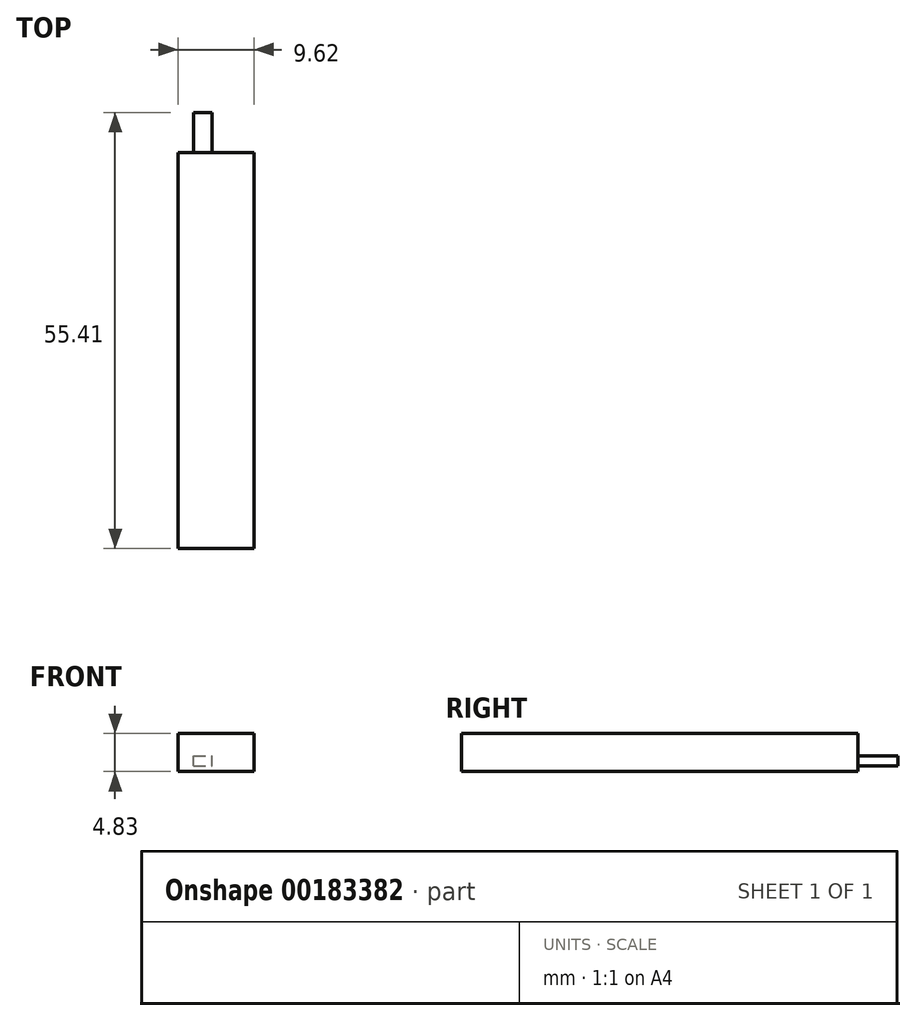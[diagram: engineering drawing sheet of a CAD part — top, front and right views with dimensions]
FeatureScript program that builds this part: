
annotation { "Feature Type Name" : "Feature", "Feature Type Description" : "" }
export const myFeature = defineFeature(function(context is Context, id is Id, definition is map)
    precondition{}
    {
        {
            var Q0;
            Q0=qCreatedBy(makeId("Top.planeOp"),FACE);
            var sketch = newSketch(context, id + "F0", { "sketchPlane" : qUnion([Q0])});
            skLineSegment(sketch, "E0.bottom", {"start": v(-36.29, 75.05) * mm, "end": v(-26.67, 75.05) * mm});
            skLineSegment(sketch, "E0.top", {"start": v(-36.29, 24.72) * mm, "end": v(-26.67, 24.72) * mm});
            skLineSegment(sketch, "E0.left", {"start": v(-36.29, 75.05) * mm, "end": v(-36.29, 24.72) * mm});
            skLineSegment(sketch, "E0.right", {"start": v(-26.67, 75.05) * mm, "end": v(-26.67, 24.72) * mm});
            skSolve(sketch);
        }
        {
            var Q0;
            Q0=makeQuery(id+"F0.imprint","IMPRINT",FACE,{"disambiguationData":[TD([[makeQuery(id+"F0.imprint","IMPRINT",EDGE,{"derivedFrom":sQuery(id+"F0.wireOp",EDGE,"E0.bottom")}),-1.0]])]});
            extrude(context, id + "F1", {"entities" : qUnion([Q0]), "depth" : 4.83 * mm});
        }
        {
            var Q0;
            Q0=makeQuery(id+"F1.opExtrude","SWEPT_FACE",FACE,{"disambiguationData":[OSD([sQuery(id+"F0.wireOp",EDGE,"E0.bottom")])]});
            var sketch = newSketch(context, id + "F2", { "sketchPlane" : qUnion([Q0])});
            skLineSegment(sketch, "E1.bottom", {"start": v(34.36, 0.7) * mm, "end": v(31.98, 0.7) * mm});
            skLineSegment(sketch, "E1.top", {"start": v(34.36, 2.02) * mm, "end": v(31.98, 2.02) * mm});
            skLineSegment(sketch, "E1.left", {"start": v(34.36, 0.7) * mm, "end": v(34.36, 2.02) * mm});
            skLineSegment(sketch, "E1.right", {"start": v(31.98, 0.7) * mm, "end": v(31.98, 2.02) * mm});
            skSolve(sketch);
        }
        {
            var Q0;
            Q0 = qSketchRegion(id + "F2", true);
            extrude(context, id + "F3", {"entities" : qUnion([Q0]), "operationType" : NewBodyOperationType.ADD, "depth" : 5.08 * mm});
        }
    });
